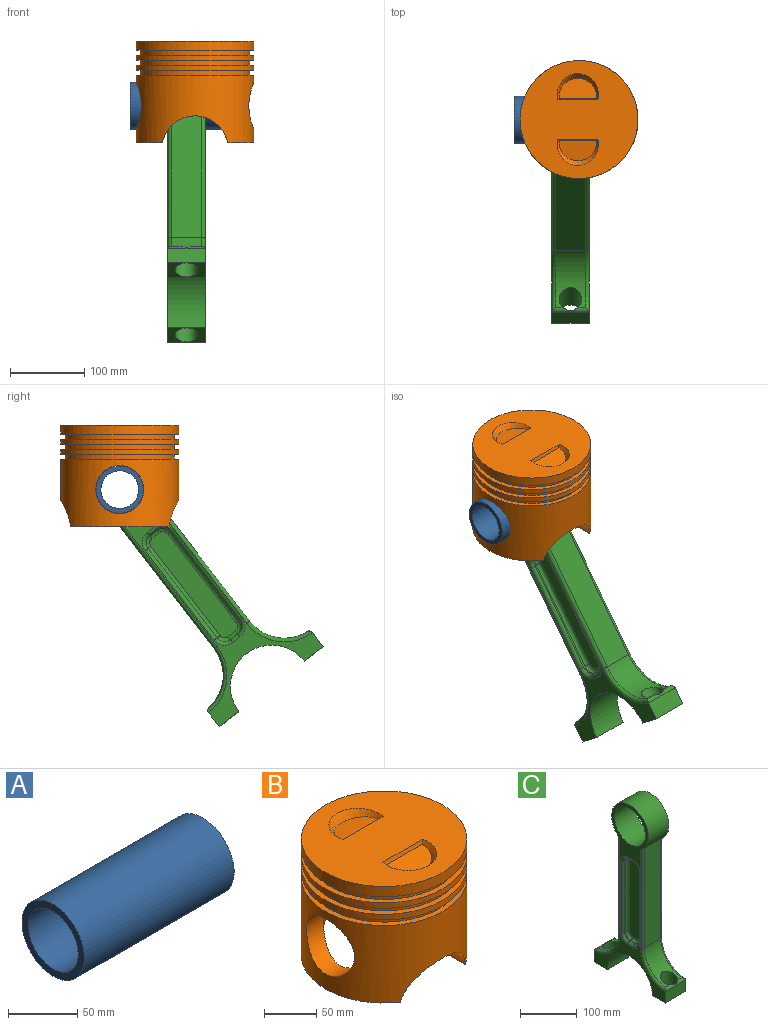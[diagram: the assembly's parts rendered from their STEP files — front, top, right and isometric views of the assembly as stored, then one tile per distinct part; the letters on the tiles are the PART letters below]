
ASSEMBLY  parts=3 mates=2
PART A: 4 faces, bbox 152.4x63.5x63.5 mm
  f0: plane 63.47x63.47mm, normal (-1,0,0), area 1139.6mm2, adj f2,f3
  f1: plane 63.47x63.47mm, normal (1,0,0), area 1139.6mm2, adj f2,f3
  f2: cylinder r=31.74mm len=152.4mm, axis (1,0,0), area 30390.3mm2, adj f0,f1
  f3: cylinder r=25.39mm len=152.4mm, axis (1,0,0), area 24309.8mm2, adj f0,f1
PART B: 28 faces, bbox 159.2x159.2x142.1 mm
  f0: plane 132.59x35.58mm, normal (0,0,-1), area 2460.5mm2, adj f16,f18,f26,f27
  f1: cone r=25.2mm half-angle=30deg, axis (0,0.14,0.99), area 727.8mm2, adj f2,f3,f14
  f2: plane 54.02x4.06mm, normal (0,0.93,0.37), area 224.1mm2, adj f1,f3,f14
  f3: plane 50.4x27.32mm, normal (0,0.14,0.99), area 1117.9mm2, adj f1,f2
  f4: plane 159.12x159.12mm, normal (0,0,-1), area 2809mm2, adj f5,f20
  f5: cylinder r=79.56mm len=159.12mm, axis (0,0,1), area 3310mm2, adj f4,f6
  f6: plane 159.12x159.12mm, normal (0,0,1), area 2809mm2, adj f5,f7
  f7: cylinder r=73.72mm len=147.45mm, axis (0,0,1), area 3310.7mm2, adj f6,f8
  f8: plane 159.12x159.12mm, normal (0,0,-1), area 2809mm2, adj f7,f9
  f9: cylinder r=79.56mm len=159.12mm, axis (0,0,1), area 3174.2mm2, adj f8,f10
  f10: plane 159.12x159.12mm, normal (0,0,1), area 2809mm2, adj f9,f11
  f11: cylinder r=73.72mm len=147.45mm, axis (0,0,1), area 3310.7mm2, adj f10,f12
  f12: plane 159.12x159.12mm, normal (0,0,-1), area 2809mm2, adj f11,f13
  f13: cylinder r=79.56mm len=159.12mm, axis (0,0,1), area 6030.8mm2, adj f12,f14
  f14: plane 159.12x159.12mm, normal (0,0,1), area 16665.4mm2, adj f1,f2,f13,f23,f24
  f15: plane 119.12x119.12mm, normal (0,0,-1), area 11143.8mm2, adj f16
  f16: cylinder r=59.56mm len=119.12mm, axis (0,0,1), area 31370.6mm2, adj f0,f15,f17,f21,f22,f26,f27
  f17: plane 132.59x35.58mm, normal (0,0,-1), area 2460.5mm2, adj f16,f18,f26,f27
  f18: cylinder r=79.56mm len=159.12mm, axis (0,0,1), area 33787.7mm2, adj f0,f17,f19,f21,f22,f26,f27
  f19: plane 159.12x159.12mm, normal (0,0,1), area 2809mm2, adj f18,f20
  f20: cylinder r=73.72mm len=147.45mm, axis (0,0,1), area 3067.3mm2, adj f4,f19
  f21: cylinder r=32.44mm len=64.89mm, axis (1,0,0), area 4337.4mm2, adj f16,f18
  f22: cylinder r=32.44mm len=64.89mm, axis (1,0,0), area 4338mm2, adj f16,f18
  f23: cone r=25.2mm half-angle=30deg, axis (0,-0.14,0.99), area 727.8mm2, adj f14,f24,f25
  f24: plane 54.02x4.06mm, normal (0,-0.93,0.37), area 224.1mm2, adj f14,f23,f25
  f25: plane 50.4x27.32mm, normal (0,-0.14,0.99), area 1117.9mm2, adj f23,f24
  f26: cylinder r=44.76mm len=87.96mm, axis (0,-1,0), area 2775.9mm2, adj f0,f16,f17,f18
  f27: cylinder r=44.76mm len=87.96mm, axis (0,-1,0), area 2776.2mm2, adj f0,f16,f17,f18
PART C: 75 faces, bbox 50.8x177.2x381 mm
  f0: cylinder r=58.7mm len=58.51mm, axis (-1,0,0), area 2812.7mm2, adj f7,f13,f16,f17,f18
  f1: cylinder r=58.7mm len=58.41mm, axis (-1,0,0), area 2787.8mm2, adj f9,f14,f21,f22,f23
  f2: plane 50.8x24.02mm, normal (0,-1,0), area 1220mm2, adj f3,f11,f12,f21,f22,f23
  f3: plane 50.8x32.31mm, normal (0,0,-1), area 911.8mm2, adj f2,f4,f11,f12,f14
  f4: cylinder r=55.64mm len=111.29mm, axis (-1,0,0), area 8880.1mm2, adj f3,f5,f11,f12
  f5: plane 50.8x33.54mm, normal (0,0,-1), area 974mm2, adj f4,f6,f11,f12,f13
  f6: plane 50.8x23.91mm, normal (0,1,0), area 1214.5mm2, adj f5,f11,f12,f16,f17,f18
  f7: plane 213.72x40.64mm, normal (0,1,0), area 8685.5mm2, adj f0,f8,f15,f19
  f8: cylinder r=45.72mm len=91.44mm, axis (-1,0,0), area 11232.4mm2, adj f7,f9,f11,f12,f15,f19,f20,f24
  f9: plane 213.72x40.64mm, normal (0,-1,0), area 8685.5mm2, adj f1,f8,f20,f24
  f10: cylinder r=38.1mm len=76.2mm, axis (-1,0,0), area 12161mm2, adj f11,f12
  f11: plane 381x177.13mm, normal (1,0,0), area 7919.6mm2, adj f2,f3,f4,f5,f6,f8,f10,f15
  f12: plane 381x177.13mm, normal (-1,0,0), area 7919.6mm2, adj f2,f3,f4,f5,f6,f8,f10,f18
  f13: cylinder r=15.24mm len=38.68mm, axis (0,0,-1), area 3112.2mm2, adj f0,f5,f17
  f14: cylinder r=15.24mm len=38.68mm, axis (0,0,-1), area 3099.2mm2, adj f1,f3,f22
  f15: cylinder r=5.08mm len=213.72mm, axis (0,0,-1), area 1693.4mm2, adj f7,f8,f11,f16
  f16: torus R=63.78mm, axis (1,0,0), area 745.7mm2, adj f0,f6,f11,f15,f17
  f17: cylinder r=5.08mm len=50.79mm, axis (-1,0,0), area 325.8mm2, adj f0,f6,f13,f16,f18
  f18: torus R=63.78mm, axis (1,0,0), area 745.7mm2, adj f0,f6,f12,f17,f19
  f19: cylinder r=5.08mm len=213.72mm, axis (0,0,1), area 1693.4mm2, adj f7,f8,f12,f18
  f20: cylinder r=5.08mm len=213.72mm, axis (0,0,1), area 1693.4mm2, adj f8,f9,f11,f21
  f21: torus R=63.78mm, axis (1,0,0), area 736.4mm2, adj f1,f2,f11,f20,f22
  f22: cylinder r=5.08mm len=50.78mm, axis (-1,0,0), area 295.2mm2, adj f1,f2,f14,f21,f23
  f23: torus R=63.78mm, axis (1,0,0), area 736.4mm2, adj f1,f2,f12,f22,f24
  f24: cylinder r=5.08mm len=213.72mm, axis (0,0,-1), area 1693.4mm2, adj f8,f9,f12,f23
  f25: plane 152.4x2.54mm, normal (0,-1,0), area 387.1mm2, adj f26,f32,f36,f44
  f26: cylinder r=12.7mm len=12.7mm, axis (-1,0,0), area 50.7mm2, adj f25,f27,f34,f42
  f27: plane 12.7x2.54mm, normal (0,0,1), area 32.3mm2, adj f26,f28,f35,f43
  f28: cylinder r=12.7mm len=12.7mm, axis (-1,0,0), area 50.7mm2, adj f27,f29,f37,f45
  f29: plane 152.4x2.54mm, normal (0,1,0), area 387.1mm2, adj f28,f30,f39,f47
  f30: cylinder r=12.7mm len=12.7mm, axis (-1,0,0), area 50.7mm2, adj f29,f31,f41,f49
  f31: plane 12.7x2.54mm, normal (0,0,-1), area 32.3mm2, adj f30,f32,f40,f48
  f32: cylinder r=12.7mm len=12.7mm, axis (-1,0,0), area 50.7mm2, adj f25,f31,f38,f46
  f33: plane 167.64x27.94mm, normal (-1,0,0), area 4634mm2, adj f42,f43,f44,f45,f46,f47,f48,f49
  f34: torus R=17.78mm, axis (1,0,0), area 182.3mm2, adj f12,f26,f35,f36
  f35: cylinder r=5.08mm len=12.7mm, axis (0,-1,0), area 101.3mm2, adj f12,f27,f34,f37
  f36: cylinder r=5.08mm len=152.4mm, axis (0,0,-1), area 1216.1mm2, adj f12,f25,f34,f38
  f37: torus R=17.78mm, axis (1,0,0), area 182.3mm2, adj f12,f28,f35,f39
  f38: torus R=17.78mm, axis (1,0,0), area 182.3mm2, adj f12,f32,f36,f40
  f39: cylinder r=5.08mm len=152.4mm, axis (0,0,1), area 1216.1mm2, adj f12,f29,f37,f41
  f40: cylinder r=5.08mm len=12.7mm, axis (0,1,0), area 101.3mm2, adj f12,f31,f38,f41
  f41: torus R=17.78mm, axis (1,0,0), area 182.3mm2, adj f12,f30,f39,f40
  f42: torus R=7.62mm, axis (-1,0,0), area 136mm2, adj f26,f33,f43,f44
  f43: cylinder r=5.08mm len=12.7mm, axis (0,-1,0), area 101.3mm2, adj f27,f33,f42,f45
  f44: cylinder r=5.08mm len=152.4mm, axis (0,0,-1), area 1216.1mm2, adj f25,f33,f42,f46
  f45: torus R=7.62mm, axis (-1,0,0), area 136mm2, adj f28,f33,f43,f47
  f46: torus R=7.62mm, axis (-1,0,0), area 136mm2, adj f32,f33,f44,f48
  f47: cylinder r=5.08mm len=152.4mm, axis (0,0,1), area 1216.1mm2, adj f29,f33,f45,f49
  f48: cylinder r=5.08mm len=12.7mm, axis (0,1,0), area 101.3mm2, adj f31,f33,f46,f49
  f49: torus R=7.62mm, axis (-1,0,0), area 136mm2, adj f30,f33,f47,f48
  f50: plane 152.4x2.54mm, normal (0,1,0), area 387.1mm2, adj f51,f57,f62,f70
  f51: cylinder r=12.7mm len=12.7mm, axis (1,0,0), area 50.7mm2, adj f50,f52,f64,f72
  f52: plane 12.7x2.54mm, normal (0,0,1), area 32.3mm2, adj f51,f53,f66,f74
  f53: cylinder r=12.7mm len=12.7mm, axis (1,0,0), area 50.7mm2, adj f52,f54,f65,f73
  f54: plane 152.4x2.54mm, normal (0,-1,0), area 387.1mm2, adj f53,f55,f63,f71
  f55: cylinder r=12.7mm len=12.7mm, axis (1,0,0), area 50.7mm2, adj f54,f56,f61,f69
  f56: plane 12.7x2.54mm, normal (0,0,-1), area 32.3mm2, adj f55,f57,f59,f67
  f57: cylinder r=12.7mm len=12.7mm, axis (1,0,0), area 50.7mm2, adj f50,f56,f60,f68
  f58: plane 167.64x27.94mm, normal (1,0,0), area 4634mm2, adj f67,f68,f69,f70,f71,f72,f73,f74
  f59: cylinder r=5.08mm len=12.7mm, axis (0,1,0), area 101.3mm2, adj f11,f56,f60,f61
  f60: torus R=17.78mm, axis (1,0,0), area 182.3mm2, adj f11,f57,f59,f62
  f61: torus R=17.78mm, axis (1,0,0), area 182.3mm2, adj f11,f55,f59,f63
  f62: cylinder r=5.08mm len=152.4mm, axis (0,0,1), area 1216.1mm2, adj f11,f50,f60,f64
  f63: cylinder r=5.08mm len=152.4mm, axis (0,0,-1), area 1216.1mm2, adj f11,f54,f61,f65
  f64: torus R=17.78mm, axis (1,0,0), area 182.3mm2, adj f11,f51,f62,f66
  f65: torus R=17.78mm, axis (1,0,0), area 182.3mm2, adj f11,f53,f63,f66
  f66: cylinder r=5.08mm len=12.7mm, axis (0,-1,0), area 101.3mm2, adj f11,f52,f64,f65
  f67: cylinder r=5.08mm len=12.7mm, axis (0,-1,0), area 101.3mm2, adj f56,f58,f68,f69
  f68: torus R=7.62mm, axis (1,0,0), area 136mm2, adj f57,f58,f67,f70
  f69: torus R=7.62mm, axis (1,0,0), area 136mm2, adj f55,f58,f67,f71
  f70: cylinder r=5.08mm len=152.4mm, axis (0,0,-1), area 1216.1mm2, adj f50,f58,f68,f72
  f71: cylinder r=5.08mm len=152.4mm, axis (0,0,1), area 1216.1mm2, adj f54,f58,f69,f73
  f72: torus R=7.62mm, axis (1,0,0), area 136mm2, adj f51,f58,f70,f74
  f73: torus R=7.62mm, axis (1,0,0), area 136mm2, adj f53,f58,f71,f74
  f74: cylinder r=5.08mm len=12.7mm, axis (0,1,0), area 101.3mm2, adj f52,f58,f72,f73
PLACE A t=(-7.08,155.17,-111.13)mm
PLACE B t=(4.39,155.17,-24.28)mm
PLACE C rot(axis=(-1,0,0),37.7deg) t=(-7.08,119.26,-157.64)mm
MATE cylindrical B.f21 <-> A.f2  axis (1,0,0) through (69.12,155.17,-111.13)mm
MATE revolute C.f8 <-> A.f2  axis (-1,0,0) through (-7.08,155.17,-111.13)mm
